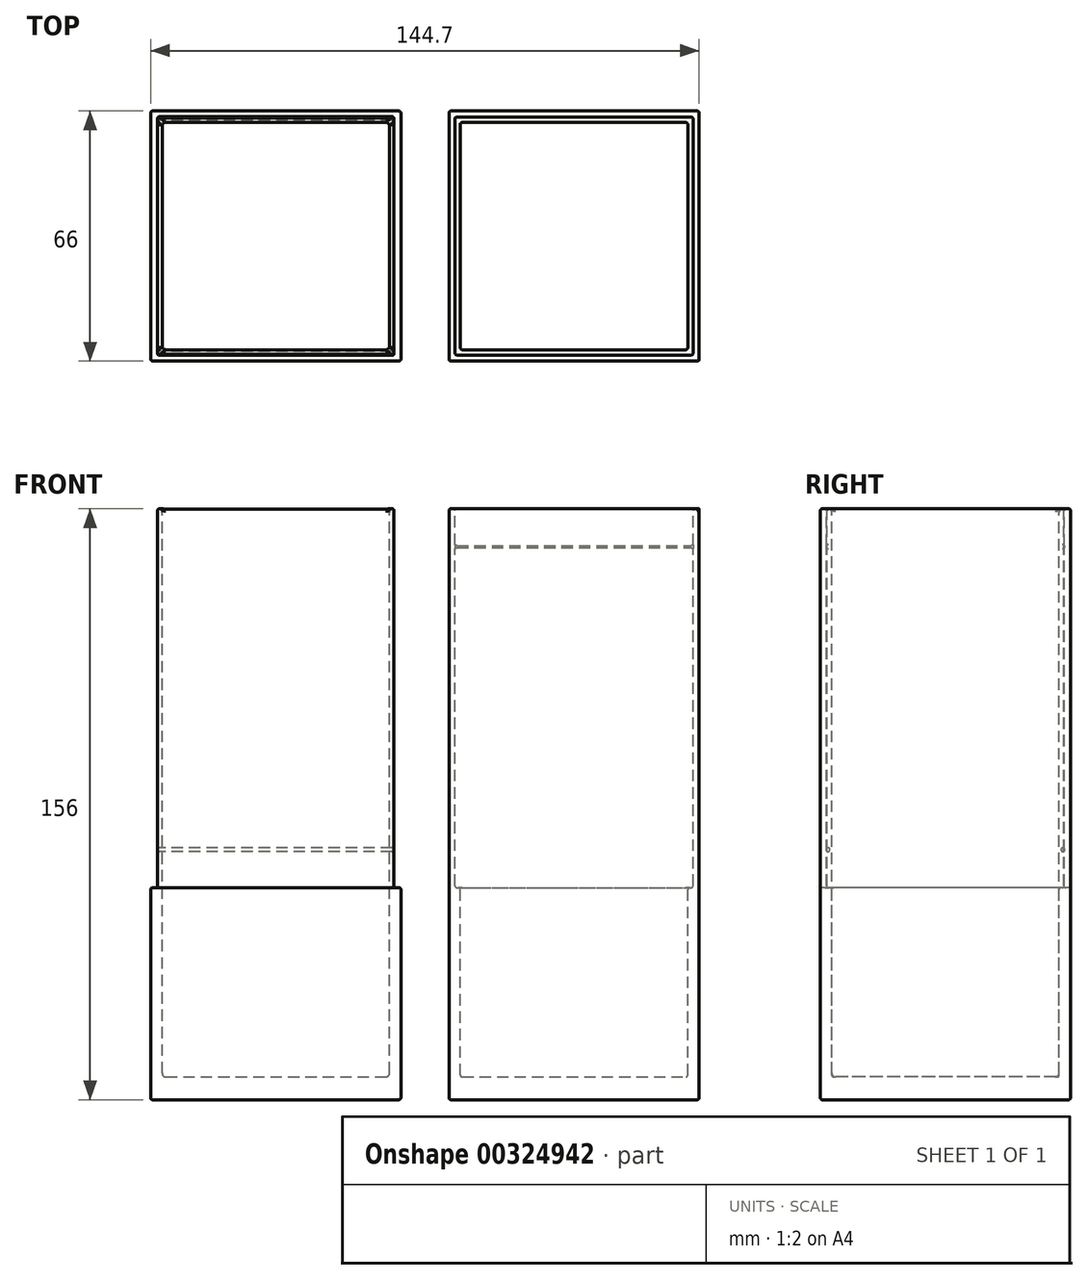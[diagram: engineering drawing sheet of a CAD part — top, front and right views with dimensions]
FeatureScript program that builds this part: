
annotation { "Feature Type Name" : "Feature", "Feature Type Description" : "" }
export const myFeature = defineFeature(function(context is Context, id is Id, definition is map)
    precondition{}
    {
        {
            var Q0;
            Q0=qCreatedBy(makeId("Front.planeOp"),FACE);
            var sketch = newSketch(context, id + "F0", { "sketchPlane" : qUnion([Q0])});
            skLineSegment(sketch, "E0.bottom", {"start": v(-66, 156) * mm, "end": v(0, 156) * mm});
            skLineSegment(sketch, "E0.top", {"start": v(-66, 0) * mm, "end": v(0, 0) * mm});
            skLineSegment(sketch, "E0.left", {"start": v(-66, 156) * mm, "end": v(-66, 0) * mm});
            skLineSegment(sketch, "E0.right", {"start": v(0, 156) * mm, "end": v(0, 0) * mm});
            skLineSegment(sketch, "E1.bottom", {"start": v(12.7, 156) * mm, "end": v(78.7, 156) * mm});
            skLineSegment(sketch, "E1.top", {"start": v(12.7, 0) * mm, "end": v(78.7, 0) * mm});
            skLineSegment(sketch, "E1.left", {"start": v(12.7, 156) * mm, "end": v(12.7, 0) * mm});
            skLineSegment(sketch, "E1.right", {"start": v(78.7, 156) * mm, "end": v(78.7, 0) * mm});
            skSolve(sketch);
        }
        {
            var Q0;
            Q0 = qSketchRegion(id + "F0", true);
            extrude(context, id + "F1", {"entities" : qUnion([Q0]), "depth" : 66 * mm, "offsetDistance" : 25 * mm});
        }
        {
            var Q0;
            Q0=makeQuery(id+"F1.opExtrude","SWEPT_FACE",FACE,{"disambiguationData":[OSD([sQuery(id+"F0.wireOp",EDGE,"E1.bottom")])]});
            var sketch = newSketch(context, id + "F2", { "sketchPlane" : qUnion([Q0])});
            skLineSegment(sketch, "E2.bottom", {"start": v(-64.2, -1.8) * mm, "end": v(-1.8, -1.8) * mm});
            skLineSegment(sketch, "E2.top", {"start": v(-64.2, -64.2) * mm, "end": v(-1.8, -64.2) * mm});
            skLineSegment(sketch, "E2.left", {"start": v(-64.2, -1.8) * mm, "end": v(-64.2, -64.2) * mm});
            skLineSegment(sketch, "E2.right", {"start": v(-1.8, -1.8) * mm, "end": v(-1.8, -64.2) * mm});
            skLineSegment(sketch, "E3.bottom", {"start": v(14.3, -1.6) * mm, "end": v(77.1, -1.6) * mm});
            skLineSegment(sketch, "E3.top", {"start": v(14.3, -64.4) * mm, "end": v(77.1, -64.4) * mm});
            skLineSegment(sketch, "E3.left", {"start": v(14.3, -1.6) * mm, "end": v(14.3, -64.4) * mm});
            skLineSegment(sketch, "E3.right", {"start": v(77.1, -1.6) * mm, "end": v(77.1, -64.4) * mm});
            skLineSegment(sketch, "E4.bottom", {"start": v(15.7, -3) * mm, "end": v(75.7, -3) * mm});
            skLineSegment(sketch, "E4.top", {"start": v(15.7, -63) * mm, "end": v(75.7, -63) * mm});
            skLineSegment(sketch, "E4.left", {"start": v(15.7, -3) * mm, "end": v(15.7, -63) * mm});
            skLineSegment(sketch, "E4.right", {"start": v(75.7, -3) * mm, "end": v(75.7, -63) * mm});
            skLineSegment(sketch, "E5.bottom", {"start": v(-66, 0) * mm, "end": v(0, 0) * mm});
            skLineSegment(sketch, "E5.top", {"start": v(-66, -66) * mm, "end": v(0, -66) * mm});
            skLineSegment(sketch, "E5.left", {"start": v(-66, 0) * mm, "end": v(-66, -66) * mm});
            skLineSegment(sketch, "E5.right", {"start": v(0, 0) * mm, "end": v(0, -66) * mm});
            skSolve(sketch);
        }
        {
            var Q0;
            Q0 = qSketchRegion(id + "F2", true);
            extrude(context, id + "F3", {"entities" : qUnion([Q0]), "operationType" : NewBodyOperationType.REMOVE, "oppositeDirection" : true, "depth" : 100 * mm, "offsetDistance" : 25 * mm});
        }
        {
            var Q0;
            Q0=makeQuery(id+"F3.boolean.opBoolean","SPLIT",FACE,{"disambiguationData":[TD([makeQuery(id+"F3.opExtrude","SWEPT_FACE",FACE,{"disambiguationData":[OSD([sQuery(id+"F2.wireOp",EDGE,"E4.bottom")])]})])],"derivedFrom":makeQuery(id+"F1.opExtrude","SWEPT_FACE",FACE,{"disambiguationData":[OSD([sQuery(id+"F0.wireOp",EDGE,"E1.bottom")])]})});
            var sketch = newSketch(context, id + "F4", { "sketchPlane" : qUnion([Q0])});
            skLineSegment(sketch, "E6.bottom", {"start": v(15.7, -3) * mm, "end": v(75.7, -3) * mm});
            skLineSegment(sketch, "E6.top", {"start": v(15.7, -63) * mm, "end": v(75.7, -63) * mm});
            skLineSegment(sketch, "E6.left", {"start": v(15.7, -3) * mm, "end": v(15.7, -63) * mm});
            skLineSegment(sketch, "E6.right", {"start": v(75.7, -3) * mm, "end": v(75.7, -63) * mm});
            skLineSegment(sketch, "E7.bottom", {"start": v(-63, -3) * mm, "end": v(-3, -3) * mm});
            skLineSegment(sketch, "E7.left", {"start": v(-63, -3) * mm, "end": v(-63, -63) * mm});
            skLineSegment(sketch, "E7.right", {"start": v(-3, -3) * mm, "end": v(-3, -63) * mm});
            skLineSegment(sketch, "E8", {"start": v(-63, -63) * mm, "end": v(-3, -63) * mm});
            skSolve(sketch);
        }
        {
            var Q0;
            Q0 = qSketchRegion(id + "F4", true);
            extrude(context, id + "F5", {"entities" : qUnion([Q0]), "operationType" : NewBodyOperationType.REMOVE, "oppositeDirection" : true, "depth" : 150 * mm, "offsetDistance" : 25 * mm});
        }
        {
            var Q0;
            Q0=makeQuery(id+"F5.boolean.opBoolean","COPY",FACE,{"derivedFrom":makeQuery(id+"F5.opExtrude","CAP_FACE",FACE,{"disambiguationData":[OSD([sQuery(id+"F4.wireOp",EDGE,"E7.bottom"),sQuery(id+"F4.wireOp",EDGE,"E7.left"),sQuery(id+"F4.wireOp",EDGE,"E7.right"),sQuery(id+"F4.wireOp",EDGE,"E8")])],"isStart":false})});
            var Q1;
            Q1=makeQuery(id+"F5.boolean.opBoolean","COPY",FACE,{"derivedFrom":makeQuery(id+"F5.opExtrude","SWEPT_FACE",FACE,{"disambiguationData":[OSD([sQuery(id+"F4.wireOp",EDGE,"E8")])]})});
            var Q2;
            Q2=makeQuery(id+"F5.boolean.opBoolean","COPY",FACE,{"derivedFrom":makeQuery(id+"F5.opExtrude","SWEPT_FACE",FACE,{"disambiguationData":[OSD([sQuery(id+"F4.wireOp",EDGE,"E7.right")])]})});
            var Q3;
            Q3=makeQuery(id+"F5.boolean.opBoolean","COPY",FACE,{"derivedFrom":makeQuery(id+"F5.opExtrude","SWEPT_FACE",FACE,{"disambiguationData":[OSD([sQuery(id+"F4.wireOp",EDGE,"E7.bottom")])]})});
            var Q4;
            Q4=makeQuery(id+"F5.boolean.opBoolean","COPY",FACE,{"derivedFrom":makeQuery(id+"F5.opExtrude","SWEPT_FACE",FACE,{"disambiguationData":[OSD([sQuery(id+"F4.wireOp",EDGE,"E7.left")])]})});
            fillet(context, id + "F6", {"entities" : qUnion([Q0, Q1, Q2, Q3, Q4]), "radius" : 1 * mm, "tangentPropagation" : true, "allowEdgeOverflow" : false});
        }
        {
            var Q0;
            Q0=makeQuery(id+"F3.boolean.opBoolean","COPY",FACE,{"derivedFrom":makeQuery(id+"F3.opExtrude","SWEPT_FACE",FACE,{"disambiguationData":[OSD([sQuery(id+"F2.wireOp",EDGE,"E2.left")])]})});
            var Q1;
            Q1=makeQuery(id+"F3.boolean.opBoolean","COPY",FACE,{"derivedFrom":makeQuery(id+"F3.opExtrude","SWEPT_FACE",FACE,{"disambiguationData":[OSD([sQuery(id+"F2.wireOp",EDGE,"E2.top")])]})});
            var Q2;
            Q2=makeQuery(id+"F3.boolean.opBoolean","COPY",FACE,{"derivedFrom":makeQuery(id+"F3.opExtrude","SWEPT_FACE",FACE,{"disambiguationData":[OSD([sQuery(id+"F2.wireOp",EDGE,"E2.right")])]})});
            var Q3;
            Q3=makeQuery(id+"F3.boolean.opBoolean","COPY",FACE,{"derivedFrom":makeQuery(id+"F3.opExtrude","SWEPT_FACE",FACE,{"disambiguationData":[OSD([sQuery(id+"F2.wireOp",EDGE,"E2.bottom")])]})});
            var Q4;
            Q4=makeQuery(id+"F1.opExtrude","CAP_FACE",FACE,{"disambiguationData":[OSD([sQuery(id+"F0.wireOp",EDGE,"E0.bottom"),sQuery(id+"F0.wireOp",EDGE,"E0.top"),sQuery(id+"F0.wireOp",EDGE,"E0.left"),sQuery(id+"F0.wireOp",EDGE,"E0.right")])],"isStart":true});
            var Q5;
            Q5=makeQuery(id+"F1.opExtrude","SWEPT_FACE",FACE,{"disambiguationData":[OSD([sQuery(id+"F0.wireOp",EDGE,"E0.left")])]});
            var Q6;
            Q6=makeQuery(id+"F1.opExtrude","CAP_FACE",FACE,{"disambiguationData":[OSD([sQuery(id+"F0.wireOp",EDGE,"E0.bottom"),sQuery(id+"F0.wireOp",EDGE,"E0.top"),sQuery(id+"F0.wireOp",EDGE,"E0.left"),sQuery(id+"F0.wireOp",EDGE,"E0.right")])],"isStart":false});
            var Q7;
            Q7=makeQuery(id+"F1.opExtrude","SWEPT_FACE",FACE,{"disambiguationData":[OSD([sQuery(id+"F0.wireOp",EDGE,"E0.right")])]});
            var Q8;
            Q8=makeQuery(id+"F1.opExtrude","SWEPT_FACE",FACE,{"disambiguationData":[OSD([sQuery(id+"F0.wireOp",EDGE,"E0.top")])]});
            var Q9;
            Q9=makeQuery(id+"F1.opExtrude","SWEPT_FACE",FACE,{"disambiguationData":[OSD([sQuery(id+"F0.wireOp",EDGE,"E1.top")])]});
            var Q10;
            Q10=makeQuery(id+"F1.opExtrude","CAP_FACE",FACE,{"disambiguationData":[OSD([sQuery(id+"F0.wireOp",EDGE,"E1.bottom"),sQuery(id+"F0.wireOp",EDGE,"E1.top"),sQuery(id+"F0.wireOp",EDGE,"E1.left"),sQuery(id+"F0.wireOp",EDGE,"E1.right")])],"isStart":false});
            var Q11;
            Q11=makeQuery(id+"F1.opExtrude","CAP_FACE",FACE,{"disambiguationData":[OSD([sQuery(id+"F0.wireOp",EDGE,"E1.bottom"),sQuery(id+"F0.wireOp",EDGE,"E1.top"),sQuery(id+"F0.wireOp",EDGE,"E1.left"),sQuery(id+"F0.wireOp",EDGE,"E1.right")])],"isStart":true});
            var Q12;
            Q12=makeQuery(id+"F1.opExtrude","SWEPT_FACE",FACE,{"disambiguationData":[OSD([sQuery(id+"F0.wireOp",EDGE,"E1.left")])]});
            var Q13;
            Q13=makeQuery(id+"F3.boolean.opBoolean","COPY",FACE,{"derivedFrom":makeQuery(id+"F3.opExtrude","SWEPT_FACE",FACE,{"disambiguationData":[OSD([sQuery(id+"F2.wireOp",EDGE,"E3.top")])]})});
            var Q14;
            Q14=makeQuery(id+"F3.boolean.opBoolean","COPY",FACE,{"derivedFrom":makeQuery(id+"F3.opExtrude","SWEPT_FACE",FACE,{"disambiguationData":[OSD([sQuery(id+"F2.wireOp",EDGE,"E3.left")])]})});
            var Q15;
            Q15=makeQuery(id+"F5.boolean.opBoolean","COPY",FACE,{"derivedFrom":makeQuery(id+"F5.opExtrude","SWEPT_FACE",FACE,{"disambiguationData":[OSD([sQuery(id+"F4.wireOp",EDGE,"E6.top")])]})});
            var Q16;
            Q16=makeQuery(id+"F5.boolean.opBoolean","COPY",FACE,{"derivedFrom":makeQuery(id+"F5.opExtrude","SWEPT_FACE",FACE,{"disambiguationData":[OSD([sQuery(id+"F4.wireOp",EDGE,"E6.left")])]})});
            var Q17;
            Q17=makeQuery(id+"F5.boolean.opBoolean","COPY",FACE,{"derivedFrom":makeQuery(id+"F5.opExtrude","CAP_FACE",FACE,{"disambiguationData":[OSD([sQuery(id+"F4.wireOp",EDGE,"E6.bottom"),sQuery(id+"F4.wireOp",EDGE,"E6.top"),sQuery(id+"F4.wireOp",EDGE,"E6.left"),sQuery(id+"F4.wireOp",EDGE,"E6.right")])],"isStart":false})});
            var Q18;
            Q18=makeQuery(id+"F5.boolean.opBoolean","COPY",FACE,{"derivedFrom":makeQuery(id+"F5.opExtrude","SWEPT_FACE",FACE,{"disambiguationData":[OSD([sQuery(id+"F4.wireOp",EDGE,"E8")])]})});
            var Q19;
            Q19=makeQuery(id+"F5.boolean.opBoolean","COPY",FACE,{"derivedFrom":makeQuery(id+"F5.opExtrude","SWEPT_FACE",FACE,{"disambiguationData":[OSD([sQuery(id+"F4.wireOp",EDGE,"E7.left")])]})});
            var Q20;
            Q20=makeQuery(id+"F5.boolean.opBoolean","COPY",FACE,{"derivedFrom":makeQuery(id+"F5.opExtrude","SWEPT_FACE",FACE,{"disambiguationData":[OSD([sQuery(id+"F4.wireOp",EDGE,"E6.bottom")])]})});
            var Q21;
            Q21=makeQuery(id+"F3.boolean.opBoolean","COPY",FACE,{"derivedFrom":makeQuery(id+"F3.opExtrude","SWEPT_FACE",FACE,{"disambiguationData":[OSD([sQuery(id+"F2.wireOp",EDGE,"E3.bottom")])]})});
            var Q22;
            Q22=makeQuery(id+"F3.boolean.opBoolean","COPY",FACE,{"derivedFrom":makeQuery(id+"F3.opExtrude","SWEPT_FACE",FACE,{"disambiguationData":[OSD([sQuery(id+"F2.wireOp",EDGE,"E3.right")])]})});
            var Q23;
            Q23=makeQuery(id+"F5.boolean.opBoolean","COPY",FACE,{"derivedFrom":makeQuery(id+"F5.opExtrude","SWEPT_FACE",FACE,{"disambiguationData":[OSD([sQuery(id+"F4.wireOp",EDGE,"E6.right")])]})});
            fillet(context, id + "F7", {"entities" : qUnion([Q0, Q1, Q2, Q3, Q4, Q5, Q6, Q7, Q8, Q9, Q10, Q11, Q12, Q13, Q14, Q15, Q16, Q17, Q18, Q19, Q20, Q21, Q22, Q23]), "radius" : 0.5 * mm, "tangentPropagation" : true, "allowEdgeOverflow" : false});
        }
        {
            var Q0;
            Q0=makeQuery(id+"F3.boolean.opBoolean","COPY",FACE,{"derivedFrom":makeQuery(id+"F3.opExtrude","SWEPT_FACE",FACE,{"disambiguationData":[OSD([sQuery(id+"F2.wireOp",EDGE,"E2.left")])]})});
            var sketch = newSketch(context, id + "F8", { "sketchPlane" : qUnion([Q0])});
            skCircle(sketch, "E9", {"center": v(2, 66) * mm, "radius": 0.5 * mm});
            skCircle(sketch, "E10", {"center": v(64, 66) * mm, "radius": 0.5 * mm});
            skSolve(sketch);
        }
        {
            var Q0;
            Q0 = qSketchRegion(id + "F8", true);
            var Q1;
            Q1=makeQuery(id+"F3.boolean.opBoolean","COPY",FACE,{"derivedFrom":makeQuery(id+"F3.opExtrude","SWEPT_FACE",FACE,{"disambiguationData":[OSD([sQuery(id+"F2.wireOp",EDGE,"E2.right")])]})});
            extrude(context, id + "F9", {"entities" : qUnion([Q0]), "endBound" : BoundingType.UP_TO_SURFACE, "oppositeDirection" : true, "depth" : 25 * mm, "endBoundEntityFace" : qUnion([Q1]), "offsetDistance" : 25 * mm});
        }
        {
            var Q0;
            Q0=makeQuery(id+"F9.opExtrude","CAP_EDGE",EDGE,{"disambiguationData":[OSD([sQuery(id+"F8.wireOp",EDGE,"E9")])],"isStart":true});
            var Q1;
            Q1=makeQuery(id+"F9.opExtrude","CAP_FACE",FACE,{"disambiguationData":[OSD([sQuery(id+"F8.wireOp",EDGE,"E10")])],"isStart":true});
            var Q2;
            Q2=makeQuery(id+"F9.opExtrude","CAP_FACE",FACE,{"disambiguationData":[OSD([sQuery(id+"F8.wireOp",EDGE,"E10")])],"isStart":false});
            var Q3;
            Q3=makeQuery(id+"F9.opExtrude","CAP_FACE",FACE,{"disambiguationData":[OSD([sQuery(id+"F8.wireOp",EDGE,"E9")])],"isStart":false});
            fillet(context, id + "F10", {"entities" : qUnion([Q0, Q1, Q2, Q3]), "radius" : 0.5 * mm, "tangentPropagation" : true, "allowEdgeOverflow" : false});
        }
        {
            var Q0;
            Q0=makeQuery(id+"F3.boolean.opBoolean","COPY",FACE,{"derivedFrom":makeQuery(id+"F3.opExtrude","SWEPT_FACE",FACE,{"disambiguationData":[OSD([sQuery(id+"F2.wireOp",EDGE,"E3.right")])]})});
            var sketch = newSketch(context, id + "F11", { "sketchPlane" : qUnion([Q0])});
            skCircle(sketch, "E11", {"center": v(64, 146) * mm, "radius": 0.5 * mm});
            skCircle(sketch, "E12", {"center": v(64, 66) * mm, "radius": 0.5 * mm, "construction": true});
            skCircle(sketch, "E13", {"center": v(2, 146) * mm, "radius": 0.5 * mm});
            skCircle(sketch, "E14", {"center": v(2, 66) * mm, "radius": 0.5 * mm, "construction": true});
            skSolve(sketch);
        }
        {
            var Q0;
            Q0 = qSketchRegion(id + "F11", true);
            var Q1;
            Q1=makeQuery(id+"F3.boolean.opBoolean","COPY",FACE,{"derivedFrom":makeQuery(id+"F3.opExtrude","SWEPT_FACE",FACE,{"disambiguationData":[OSD([sQuery(id+"F2.wireOp",EDGE,"E3.left")])]})});
            extrude(context, id + "F12", {"entities" : qUnion([Q0]), "operationType" : NewBodyOperationType.REMOVE, "endBound" : BoundingType.UP_TO_SURFACE, "depth" : 25 * mm, "endBoundEntityFace" : qUnion([Q1]), "offsetDistance" : 25 * mm});
        }
    });
